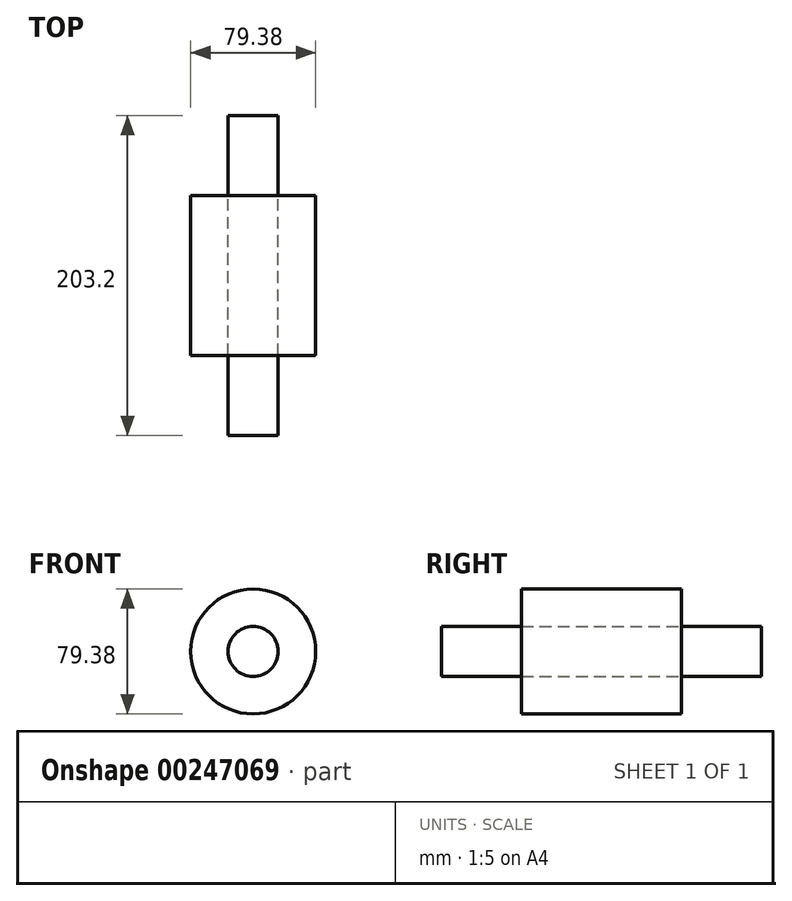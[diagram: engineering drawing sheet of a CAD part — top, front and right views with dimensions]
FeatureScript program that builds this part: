
annotation { "Feature Type Name" : "Feature", "Feature Type Description" : "" }
export const myFeature = defineFeature(function(context is Context, id is Id, definition is map)
    precondition{}
    {
        {
            var Q0;
            Q0=qCreatedBy(makeId("Front.planeOp"),FACE);
            var sketch = newSketch(context, id + "F0", { "sketchPlane" : qUnion([Q0])});
            skCircle(sketch, "E0", {"center": v(0, 0) * mm, "radius": 39.69 * mm});
            skCircle(sketch, "E1", {"center": v(0, 0) * mm, "radius": 15.88 * mm});
            skSolve(sketch);
        }
        {
            var Q0;
            Q0 = qSketchRegion(id + "F0", true);
            var Q1;
            Q1=makeQuery(id+"F0.imprint","IMPRINT",FACE,{"disambiguationData":[TD([[makeQuery(id+"F0.imprint","IMPRINT",EDGE,{"derivedFrom":sQuery(id+"F0.wireOp",EDGE,"E1")}),1.0]])]});
            extrude(context, id + "F1", {"entities" : qUnion([Q0, Q1]), "endBound" : BoundingType.SYMMETRIC, "depth" : 101.6 * mm});
        }
        {
            var Q0;
            Q0=makeQuery(id+"F0.imprint","IMPRINT",FACE,{"disambiguationData":[TD([[makeQuery(id+"F0.imprint","IMPRINT",EDGE,{"derivedFrom":sQuery(id+"F0.wireOp",EDGE,"E1")}),1.0]])]});
            extrude(context, id + "F2", {"entities" : qUnion([Q0]), "endBound" : BoundingType.SYMMETRIC, "depth" : 203.2 * mm});
        }
    });
